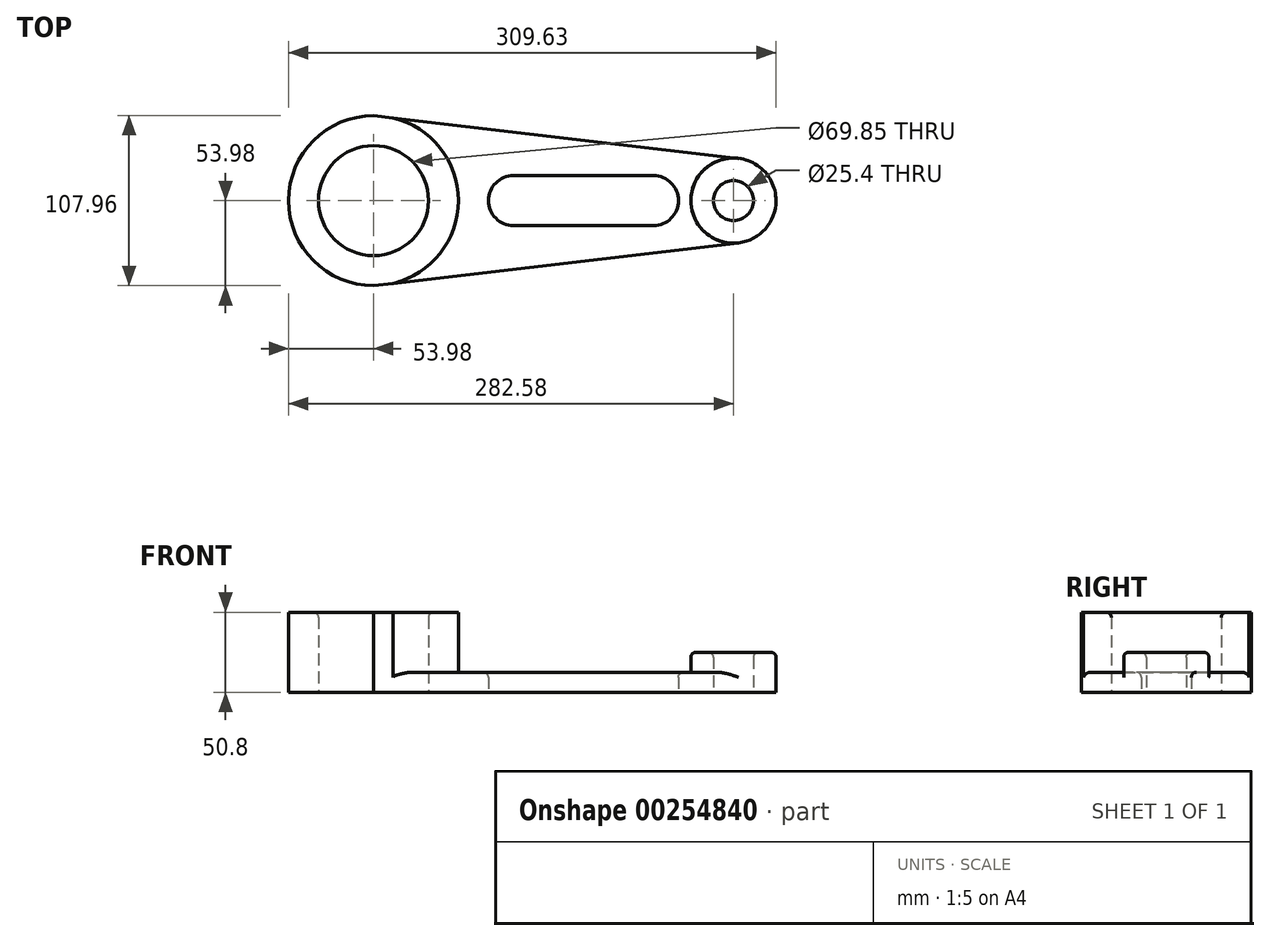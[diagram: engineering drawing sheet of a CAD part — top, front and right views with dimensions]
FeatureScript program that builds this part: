
annotation { "Feature Type Name" : "Feature", "Feature Type Description" : "" }
export const myFeature = defineFeature(function(context is Context, id is Id, definition is map)
    precondition{}
    {
        {
            var Q0;
            Q0=qCreatedBy(makeId("Top.planeOp"),FACE);
            var sketch = newSketch(context, id + "F0", { "sketchPlane" : qUnion([Q0])});
            skCircle(sketch, "E0", {"center": v(0, 0) * mm, "radius": 34.93 * mm});
            skCircle(sketch, "E1", {"center": v(0, 0) * mm, "radius": 53.98 * mm});
            skArc(sketch, "E2", {"start": v(88.9, 15.87) * mm, "mid": v(73.03, 0) * mm, "end": v(88.9, -15.88) * mm});
            skArc(sketch, "E3", {"start": v(177.8, -15.88) * mm, "mid": v(193.68, 0) * mm, "end": v(177.8, 15.87) * mm});
            skCircle(sketch, "E4", {"center": v(228.6, 0) * mm, "radius": 27.05 * mm});
            skCircle(sketch, "E5", {"center": v(228.6, 0) * mm, "radius": 12.7 * mm});
            skLineSegment(sketch, "E6", {"start": v(0, -53.97) * mm, "end": v(231.74, -26.87) * mm});
            skLineSegment(sketch, "E7", {"start": v(0, 53.97) * mm, "end": v(231.74, 26.87) * mm});
            skLineSegment(sketch, "E8", {"start": v(88.9, 15.88) * mm, "end": v(177.8, 15.88) * mm});
            skLineSegment(sketch, "E9", {"start": v(88.9, -15.88) * mm, "end": v(177.8, -15.88) * mm});
            skSolve(sketch);
        }
        {
            var Q0;
            Q0=makeQuery(id+"F0.imprint","IMPRINT",FACE,{"disambiguationData":[TD([[makeQuery(id+"F0.imprint","IMPRINT",EDGE,{"derivedFrom":sQuery(id+"F0.wireOp",EDGE,"E0")}),-1.0]])]});
            extrude(context, id + "F1", {"entities" : qUnion([Q0]), "depth" : 50.8 * mm});
        }
        {
            var Q0;
            Q0=makeQuery(id+"F0.imprint","IMPRINT",FACE,{"disambiguationData":[TD([[makeQuery(id+"F0.imprint","IMPRINT",EDGE,{"derivedFrom":sQuery(id+"F0.wireOp",EDGE,"E2")}),-1.0]])]});
            extrude(context, id + "F2", {"entities" : qUnion([Q0]), "operationType" : NewBodyOperationType.ADD, "depth" : 12.7 * mm});
        }
        {
            var Q0;
            Q0=makeQuery(id+"F0.imprint","IMPRINT",FACE,{"disambiguationData":[TD([[makeQuery(id+"F0.imprint","IMPRINT",EDGE,{"derivedFrom":sQuery(id+"F0.wireOp",EDGE,"E5")}),-1.0]])]});
            extrude(context, id + "F3", {"entities" : qUnion([Q0]), "operationType" : NewBodyOperationType.ADD, "depth" : 25.4 * mm});
        }
        {
            var Q0;
            {var subQ0=sQuery(id+"F0.wireOp",EDGE,"E1");Q0=makeQuery(id+"F1.opExtrude","CAP_EDGE",EDGE,{"disambiguationData":[OSD([subQ0]),TDD([makeQuery(id+"F0.imprint","IMPRINT",EDGE,{"disambiguationData":[TD([[makeQuery(id+"F0.imprint","INTERSECT",VERTEX,{"disambiguationData":[OD(0.0)],"derivedFrom":[subQ0,sQuery(id+"F0.wireOp",EDGE,"E6")]}),1.0]])],"derivedFrom":subQ0})])],"isStart":false});}
            var Q1;
            Q1=makeQuery(id+"F2.opExtrude","CAP_EDGE",EDGE,{"disambiguationData":[OSD([sQuery(id+"F0.wireOp",EDGE,"E7")])],"isStart":false});
            var Q2;
            Q2=makeQuery(id+"F2.opExtrude","CAP_EDGE",EDGE,{"disambiguationData":[OSD([sQuery(id+"F0.wireOp",EDGE,"E6")])],"isStart":false});
            var Q3;
            Q3=makeQuery(id+"F3.opExtrude","CAP_EDGE",EDGE,{"disambiguationData":[OSD([sQuery(id+"F0.wireOp",EDGE,"E4")])],"isStart":false});
            fillet(context, id + "F4", {"entities" : qUnion([Q0, Q1, Q2, Q3]), "radius" : 3.17 * mm, "tangentPropagation" : true, "allowEdgeOverflow" : false});
        }
        {
            var Q0;
            Q0=makeQuery(id+"F1.opExtrude","CAP_EDGE",EDGE,{"disambiguationData":[OSD([sQuery(id+"F0.wireOp",EDGE,"E0")])],"isStart":false});
            var Q1;
            Q1=makeQuery(id+"F2.opExtrude","CAP_EDGE",EDGE,{"disambiguationData":[OSD([sQuery(id+"F0.wireOp",EDGE,"E8")])],"isStart":false});
            var Q2;
            Q2=makeQuery(id+"F3.opExtrude","CAP_EDGE",EDGE,{"disambiguationData":[OSD([sQuery(id+"F0.wireOp",EDGE,"E5")])],"isStart":false});
            fillet(context, id + "F5", {"entities" : qUnion([Q0, Q1, Q2]), "radius" : 3.17 * mm, "tangentPropagation" : true, "allowEdgeOverflow" : false});
        }
    });
